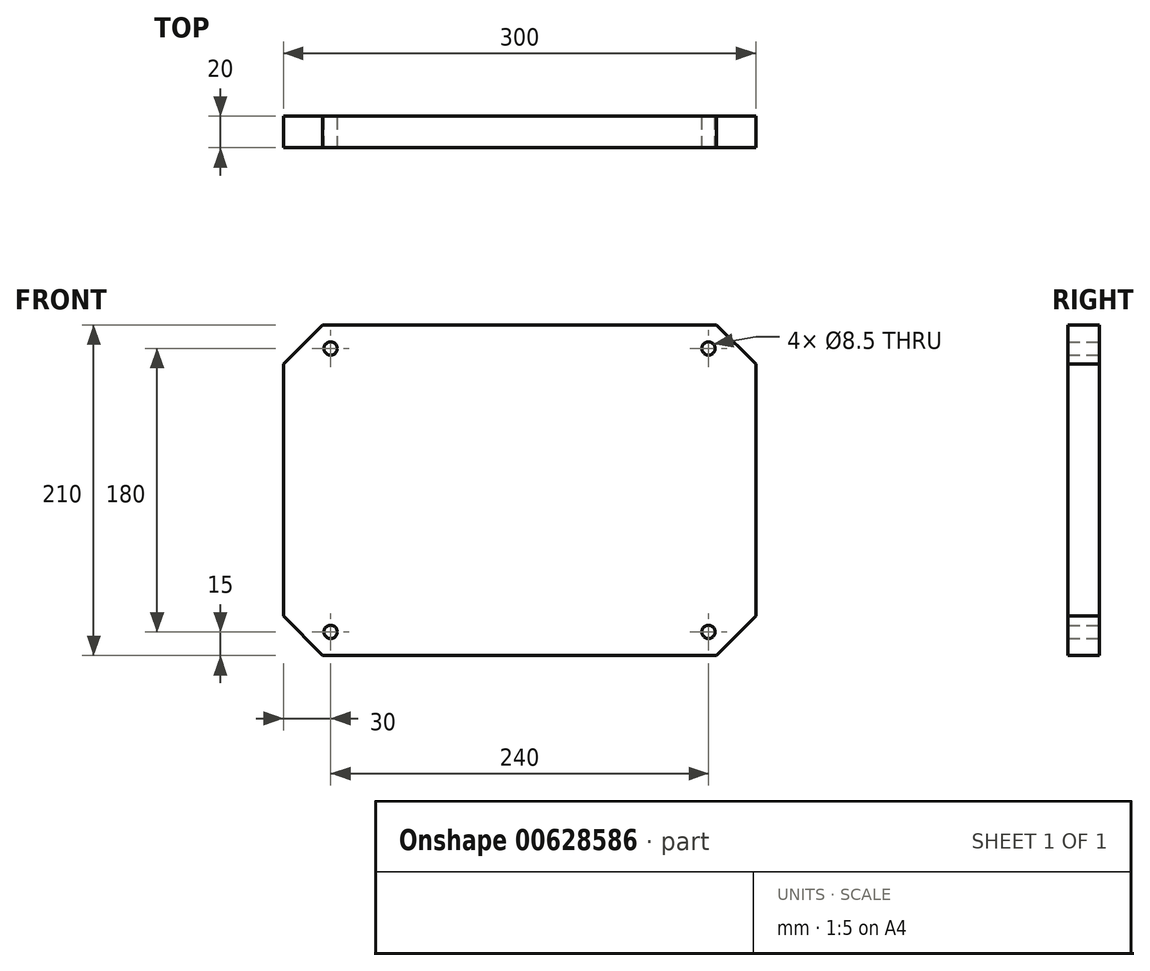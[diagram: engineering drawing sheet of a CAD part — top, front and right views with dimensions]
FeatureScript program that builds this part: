
annotation { "Feature Type Name" : "Feature", "Feature Type Description" : "" }
export const myFeature = defineFeature(function(context is Context, id is Id, definition is map)
    precondition{}
    {
        {
            var Q0;
            Q0=qCreatedBy(makeId("Front.planeOp"),FACE);
            var sketch = newSketch(context, id + "F0", { "sketchPlane" : qUnion([Q0])});
            skLineSegment(sketch, "E0.bottom", {"start": v(-150, 105) * mm, "end": v(150, 105) * mm});
            skLineSegment(sketch, "E0.top", {"start": v(-150, -105) * mm, "end": v(150, -105) * mm});
            skLineSegment(sketch, "E0.left", {"start": v(-150, 105) * mm, "end": v(-150, -105) * mm});
            skLineSegment(sketch, "E0.right", {"start": v(150, 105) * mm, "end": v(150, -105) * mm});
            skPoint(sketch, "E0.middle", {"position": v(0, 0) * mm});
            skLineSegment(sketch, "E1", {"start": v(0, 0) * mm, "end": v(189.29, 0) * mm, "construction": true});
            skLineSegment(sketch, "E2", {"start": v(0, 0) * mm, "end": v(0, 155.62) * mm, "construction": true});
            skPoint(sketch, "E2.endSnap0", {"position": v(0, 105) * mm});
            skCircle(sketch, "E3", {"center": v(120, 90) * mm, "radius": 4.25 * mm});
            skCircle(sketch, "E4.MirrorC", {"center": v(-120, 90) * mm, "radius": 4.25 * mm});
            skCircle(sketch, "E5.MirrorC", {"center": v(120, -90) * mm, "radius": 4.25 * mm});
            skCircle(sketch, "E6.MirrorC", {"center": v(-120, -90) * mm, "radius": 4.25 * mm});
            skSolve(sketch);
        }
        {
            var Q0;
            Q0 = qSketchRegion(id + "F0", true);
            extrude(context, id + "F1", {"entities" : qUnion([Q0]), "depth" : 20 * mm, "offsetDistance" : 25 * mm});
        }
        {
            var Q0;
            Q0=makeQuery(id+"F1.opExtrude","SWEPT_EDGE",EDGE,{"disambiguationData":[OSD([sQuery(id+"F0.wireOp",EDGE,"E0.bottom"),sQuery(id+"F0.wireOp",EDGE,"E0.right")])]});
            var Q1;
            Q1=makeQuery(id+"F1.opExtrude","SWEPT_EDGE",EDGE,{"disambiguationData":[OSD([sQuery(id+"F0.wireOp",EDGE,"E0.top"),sQuery(id+"F0.wireOp",EDGE,"E0.right")])]});
            var Q2;
            Q2=makeQuery(id+"F1.opExtrude","SWEPT_EDGE",EDGE,{"disambiguationData":[OSD([sQuery(id+"F0.wireOp",EDGE,"E0.top"),sQuery(id+"F0.wireOp",EDGE,"E0.left")])]});
            var Q3;
            Q3=makeQuery(id+"F1.opExtrude","SWEPT_EDGE",EDGE,{"disambiguationData":[OSD([sQuery(id+"F0.wireOp",EDGE,"E0.bottom"),sQuery(id+"F0.wireOp",EDGE,"E0.left")])]});
            chamfer(context, id + "F2", {"entities" : qUnion([Q0, Q1, Q2, Q3]), "width" : 25 * mm, "tangentPropagation" : true});
        }
    });
